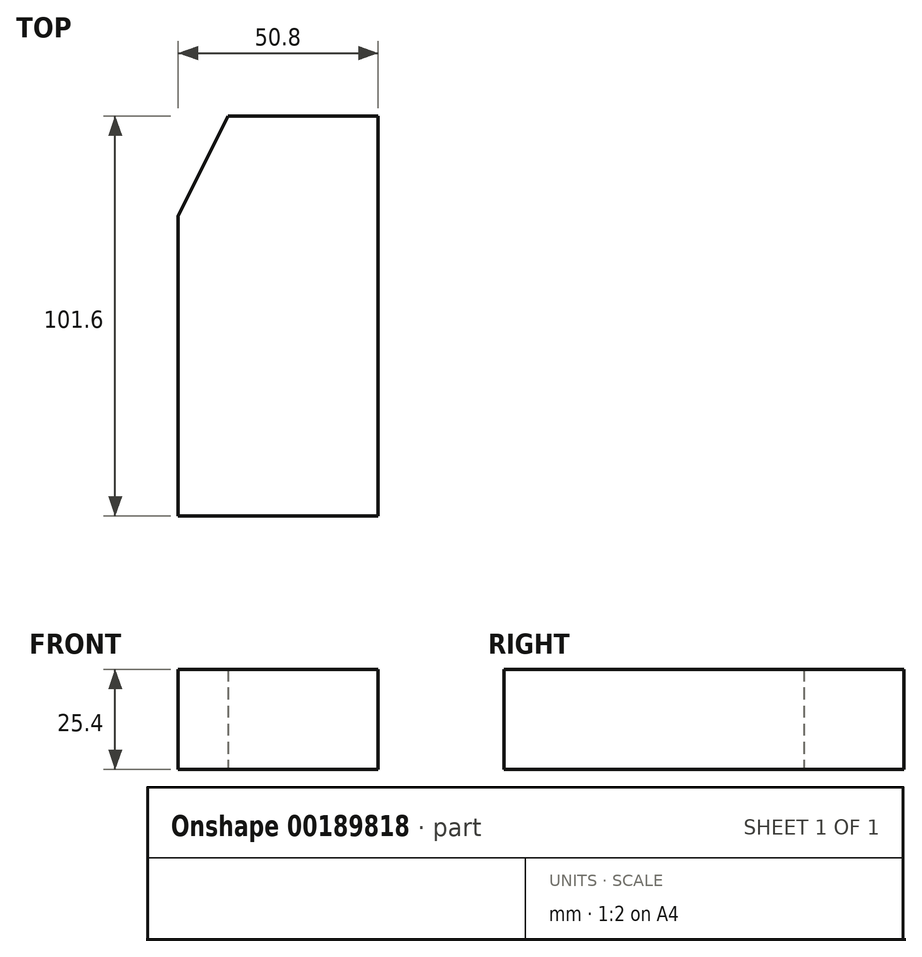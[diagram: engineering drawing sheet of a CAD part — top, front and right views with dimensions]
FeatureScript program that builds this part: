
annotation { "Feature Type Name" : "Feature", "Feature Type Description" : "" }
export const myFeature = defineFeature(function(context is Context, id is Id, definition is map)
    precondition{}
    {
        {
            var Q0;
            Q0=qCreatedBy(makeId("Top.planeOp"),FACE);
            var sketch = newSketch(context, id + "F0", { "sketchPlane" : qUnion([Q0])});
            skLineSegment(sketch, "E0.bottom", {"start": v(-25.4, -50.8) * mm, "end": v(25.4, -50.8) * mm});
            skLineSegment(sketch, "E0.top", {"start": v(-12.7, 50.8) * mm, "end": v(25.4, 50.8) * mm});
            skLineSegment(sketch, "E0.left", {"start": v(-25.4, -50.8) * mm, "end": v(-25.4, 25.4) * mm});
            skLineSegment(sketch, "E0.right", {"start": v(25.4, -50.8) * mm, "end": v(25.4, 50.8) * mm});
            skLineSegment(sketch, "E1", {"start": v(-25.4, 25.4) * mm, "end": v(-12.7, 50.8) * mm});
            skSolve(sketch);
        }
        {
            var Q0;
            Q0 = qSketchRegion(id + "F0", true);
            extrude(context, id + "F1", {"entities" : qUnion([Q0]), "depth" : 25.4 * mm});
        }
    });
